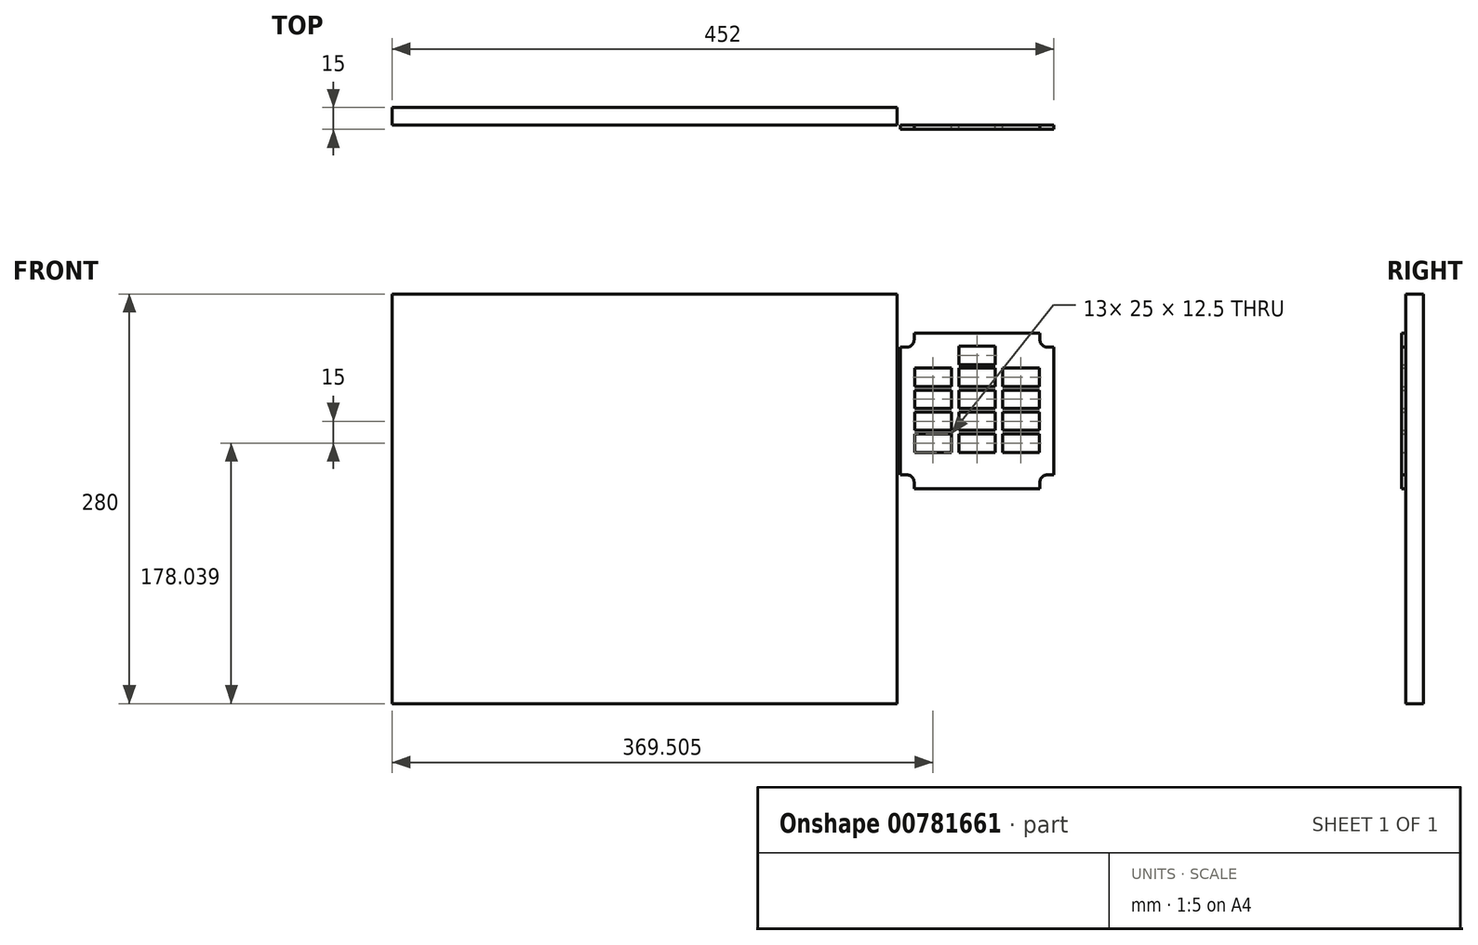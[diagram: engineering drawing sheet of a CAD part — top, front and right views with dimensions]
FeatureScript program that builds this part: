
annotation { "Feature Type Name" : "Feature", "Feature Type Description" : "" }
export const myFeature = defineFeature(function(context is Context, id is Id, definition is map)
    precondition{}
    {
        {
            var Q0;
            Q0=qCreatedBy(makeId("Front.planeOp"),FACE);
            var sketch = newSketch(context, id + "F0", { "sketchPlane" : qUnion([Q0])});
            skLineSegment(sketch, "E0.bottom", {"start": v(172.5, 140) * mm, "end": v(-172.5, 140) * mm});
            skLineSegment(sketch, "E0.top", {"start": v(172.5, -140) * mm, "end": v(-172.5, -140) * mm});
            skLineSegment(sketch, "E0.left", {"start": v(172.5, 140) * mm, "end": v(172.5, -140) * mm});
            skLineSegment(sketch, "E0.right", {"start": v(-172.5, 140) * mm, "end": v(-172.5, -140) * mm});
            skPoint(sketch, "E0.middle", {"position": v(0, 0) * mm});
            skSolve(sketch);
        }
        {
            var Q0;
            Q0=makeQuery(id+"F0.imprint","IMPRINT",FACE,{"disambiguationData":[TD([[makeQuery(id+"F0.imprint","IMPRINT",EDGE,{"derivedFrom":sQuery(id+"F0.wireOp",EDGE,"E0.bottom")}),1.0]])]});
            extrude(context, id + "F1", {"entities" : qUnion([Q0]), "oppositeDirection" : true, "depth" : 12 * mm, "offsetDistance" : 25 * mm});
        }
        {
            var Q0;
            Q0=qCreatedBy(makeId("Front.planeOp"),FACE);
            var sketch = newSketch(context, id + "F2", { "sketchPlane" : qUnion([Q0])});
            skLineSegment(sketch, "E1.bottom", {"start": v(184.03, 113.29) * mm, "end": v(269.98, 113.29) * mm});
            skLineSegment(sketch, "E1.top", {"start": v(184.03, 6.79) * mm, "end": v(269.98, 6.79) * mm});
            skLineSegment(sketch, "E1.left", {"start": v(174.5, 103.76) * mm, "end": v(174.5, 16.31) * mm});
            skLineSegment(sketch, "E1.right", {"start": v(279.5, 103.76) * mm, "end": v(279.5, 16.31) * mm});
            skLineSegment(sketch, "E2.bottom", {"start": v(214.5, 104.29) * mm, "end": v(239.5, 104.29) * mm});
            skLineSegment(sketch, "E2.top", {"start": v(214.5, 91.79) * mm, "end": v(239.5, 91.79) * mm});
            skLineSegment(sketch, "E2.left", {"start": v(214.5, 104.29) * mm, "end": v(214.5, 91.79) * mm});
            skLineSegment(sketch, "E2.right", {"start": v(239.5, 104.29) * mm, "end": v(239.5, 91.79) * mm});
            skLineSegment(sketch, "E3", {"start": v(227, 104.29) * mm, "end": v(227, 102.79) * mm});
            skLineSegment(sketch, "E4.0.1.0", {"start": v(214.5, 89.29) * mm, "end": v(239.5, 89.29) * mm});
            skLineSegment(sketch, "E4.0.1.1", {"start": v(214.5, 89.29) * mm, "end": v(214.5, 76.79) * mm});
            skLineSegment(sketch, "E4.0.1.2", {"start": v(214.5, 76.79) * mm, "end": v(239.5, 76.79) * mm});
            skLineSegment(sketch, "E4.0.1.3", {"start": v(239.5, 89.29) * mm, "end": v(239.5, 76.79) * mm});
            skLineSegment(sketch, "E4.0.2.0", {"start": v(214.5, 74.29) * mm, "end": v(239.5, 74.29) * mm});
            skLineSegment(sketch, "E4.0.2.1", {"start": v(214.5, 74.29) * mm, "end": v(214.5, 61.79) * mm});
            skLineSegment(sketch, "E4.0.2.2", {"start": v(214.5, 61.79) * mm, "end": v(239.5, 61.79) * mm});
            skLineSegment(sketch, "E4.0.2.3", {"start": v(239.5, 74.29) * mm, "end": v(239.5, 61.79) * mm});
            skLineSegment(sketch, "E4.0.3.0", {"start": v(214.5, 59.29) * mm, "end": v(239.5, 59.29) * mm});
            skLineSegment(sketch, "E4.0.3.1", {"start": v(214.5, 59.29) * mm, "end": v(214.5, 46.79) * mm});
            skLineSegment(sketch, "E4.0.3.2", {"start": v(214.5, 46.79) * mm, "end": v(239.5, 46.79) * mm});
            skLineSegment(sketch, "E4.0.3.3", {"start": v(239.5, 59.29) * mm, "end": v(239.5, 46.79) * mm});
            skLineSegment(sketch, "E4.0.4.0", {"start": v(214.5, 44.29) * mm, "end": v(239.5, 44.29) * mm});
            skLineSegment(sketch, "E4.0.4.1", {"start": v(214.5, 44.29) * mm, "end": v(214.5, 31.79) * mm});
            skLineSegment(sketch, "E4.0.4.2", {"start": v(214.5, 31.79) * mm, "end": v(239.5, 31.79) * mm});
            skLineSegment(sketch, "E4.0.4.3", {"start": v(239.5, 44.29) * mm, "end": v(239.5, 31.79) * mm});
            skLineSegment(sketch, "E4.direction1", {"start": v(214.5, 104.29) * mm, "end": v(239.5, 104.29) * mm, "construction": true});
            skLineSegment(sketch, "E4.direction2", {"start": v(214.5, 104.29) * mm, "end": v(214.5, 89.29) * mm, "construction": true});
            skLineSegment(sketch, "E5.1.0.0", {"start": v(244.5, 89.29) * mm, "end": v(244.5, 76.79) * mm});
            skLineSegment(sketch, "E5.1.0.1", {"start": v(244.5, 89.29) * mm, "end": v(269.5, 89.29) * mm});
            skLineSegment(sketch, "E5.1.0.2", {"start": v(244.5, 74.29) * mm, "end": v(269.5, 74.29) * mm});
            skLineSegment(sketch, "E5.1.0.3", {"start": v(244.5, 61.79) * mm, "end": v(269.5, 61.79) * mm});
            skLineSegment(sketch, "E5.1.0.4", {"start": v(244.5, 76.79) * mm, "end": v(269.5, 76.79) * mm});
            skLineSegment(sketch, "E5.1.0.5", {"start": v(244.5, 74.29) * mm, "end": v(244.5, 61.79) * mm});
            skLineSegment(sketch, "E5.1.0.6", {"start": v(269.5, 89.29) * mm, "end": v(269.5, 76.79) * mm});
            skLineSegment(sketch, "E5.1.0.7", {"start": v(269.5, 44.29) * mm, "end": v(269.5, 31.79) * mm});
            skLineSegment(sketch, "E5.1.0.8", {"start": v(244.5, 31.79) * mm, "end": v(269.5, 31.79) * mm});
            skLineSegment(sketch, "E5.1.0.9", {"start": v(244.5, 44.29) * mm, "end": v(244.5, 31.79) * mm});
            skLineSegment(sketch, "E5.1.0.10", {"start": v(244.5, 44.29) * mm, "end": v(269.5, 44.29) * mm});
            skLineSegment(sketch, "E5.1.0.11", {"start": v(269.5, 59.29) * mm, "end": v(269.5, 46.79) * mm});
            skLineSegment(sketch, "E5.1.0.12", {"start": v(244.5, 46.79) * mm, "end": v(269.5, 46.79) * mm});
            skLineSegment(sketch, "E5.1.0.13", {"start": v(244.5, 59.29) * mm, "end": v(244.5, 46.79) * mm});
            skLineSegment(sketch, "E5.1.0.14", {"start": v(244.5, 59.29) * mm, "end": v(269.5, 59.29) * mm});
            skLineSegment(sketch, "E5.1.0.15", {"start": v(269.5, 74.29) * mm, "end": v(269.5, 61.79) * mm});
            skLineSegment(sketch, "E5.direction1", {"start": v(214.5, 31.79) * mm, "end": v(244.5, 31.79) * mm, "construction": true});
            skLineSegment(sketch, "E6.1.0.0", {"start": v(184.5, 74.29) * mm, "end": v(209.5, 74.29) * mm});
            skLineSegment(sketch, "E6.1.0.1", {"start": v(184.5, 61.79) * mm, "end": v(209.5, 61.79) * mm});
            skLineSegment(sketch, "E6.1.0.2", {"start": v(184.5, 89.29) * mm, "end": v(184.5, 76.79) * mm});
            skLineSegment(sketch, "E6.1.0.3", {"start": v(209.5, 44.29) * mm, "end": v(209.5, 31.79) * mm});
            skLineSegment(sketch, "E6.1.0.4", {"start": v(209.5, 89.29) * mm, "end": v(209.5, 76.79) * mm});
            skLineSegment(sketch, "E6.1.0.5", {"start": v(184.5, 89.29) * mm, "end": v(209.5, 89.29) * mm});
            skLineSegment(sketch, "E6.1.0.6", {"start": v(184.5, 31.79) * mm, "end": v(209.5, 31.79) * mm});
            skLineSegment(sketch, "E6.1.0.7", {"start": v(184.5, 44.29) * mm, "end": v(184.5, 31.79) * mm});
            skLineSegment(sketch, "E6.1.0.8", {"start": v(184.5, 74.29) * mm, "end": v(184.5, 61.79) * mm});
            skLineSegment(sketch, "E6.1.0.9", {"start": v(184.5, 76.79) * mm, "end": v(209.5, 76.79) * mm});
            skLineSegment(sketch, "E6.1.0.10", {"start": v(184.5, 44.29) * mm, "end": v(209.5, 44.29) * mm});
            skLineSegment(sketch, "E6.1.0.11", {"start": v(209.5, 59.29) * mm, "end": v(209.5, 46.79) * mm});
            skLineSegment(sketch, "E6.1.0.12", {"start": v(184.5, 46.79) * mm, "end": v(209.5, 46.79) * mm});
            skLineSegment(sketch, "E6.1.0.13", {"start": v(184.5, 59.29) * mm, "end": v(184.5, 46.79) * mm});
            skLineSegment(sketch, "E6.1.0.14", {"start": v(184.5, 59.29) * mm, "end": v(209.5, 59.29) * mm});
            skLineSegment(sketch, "E6.1.0.15", {"start": v(209.5, 74.29) * mm, "end": v(209.5, 61.79) * mm});
            skLineSegment(sketch, "E6.direction1", {"start": v(214.5, 31.79) * mm, "end": v(184.5, 31.79) * mm, "construction": true});
            skLineSegment(sketch, "E7", {"start": v(184.03, 113.29) * mm, "end": v(184.03, 108.53) * mm});
            skLineSegment(sketch, "E8", {"start": v(174.5, 60.04) * mm, "end": v(176.1, 60.04) * mm});
            skArc(sketch, "E9", {"start": v(179.27, 103.76) * mm, "mid": v(182.64, 105.16) * mm, "end": v(184.03, 108.53) * mm});
            skPoint(sketch, "E9.centerSnap0", {"position": v(179.27, 103.76) * mm});
            skPoint(sketch, "E9.centerSnap1", {"position": v(184.03, 108.53) * mm});
            skPoint(sketch, "E10.orphan", {"position": v(174.5, 113.29) * mm});
            skPoint(sketch, "E11.orphan", {"position": v(184.03, 103.76) * mm});
            skLineSegment(sketch, "E12", {"start": v(179.27, 103.76) * mm, "end": v(174.5, 103.76) * mm});
            skArc(sketch, "E13.MirrorCS", {"start": v(274.74, 103.76) * mm, "mid": v(271.37, 105.16) * mm, "end": v(269.98, 108.53) * mm});
            skPoint(sketch, "E14.MirrorP", {"position": v(269.98, 103.76) * mm});
            skPoint(sketch, "E15.MirrorP", {"position": v(269.98, 108.53) * mm});
            skLineSegment(sketch, "E16.MirrorCS", {"start": v(269.98, 113.29) * mm, "end": v(269.98, 108.53) * mm});
            skLineSegment(sketch, "E17.MirrorCS", {"start": v(274.74, 103.76) * mm, "end": v(279.5, 103.76) * mm});
            skPoint(sketch, "E18.MirrorP", {"position": v(274.74, 103.76) * mm});
            skPoint(sketch, "E19.MirrorP", {"position": v(279.5, 113.29) * mm});
            skLineSegment(sketch, "E20.MirrorCS", {"start": v(184.03, 6.79) * mm, "end": v(184.03, 11.55) * mm});
            skLineSegment(sketch, "E21.MirrorCS", {"start": v(179.27, 16.31) * mm, "end": v(174.5, 16.31) * mm});
            skPoint(sketch, "E22.MirrorP", {"position": v(179.27, 16.31) * mm});
            skPoint(sketch, "E23.MirrorP", {"position": v(184.03, 16.31) * mm});
            skPoint(sketch, "E24.MirrorP", {"position": v(184.03, 11.55) * mm});
            skArc(sketch, "E25.MirrorCS", {"start": v(179.27, 16.31) * mm, "mid": v(182.64, 14.92) * mm, "end": v(184.03, 11.55) * mm});
            skPoint(sketch, "E26.MirrorP", {"position": v(174.5, 6.79) * mm});
            skArc(sketch, "E27.MirrorCS", {"start": v(274.74, 16.31) * mm, "mid": v(271.37, 14.92) * mm, "end": v(269.98, 11.55) * mm});
            skPoint(sketch, "E28.MirrorP", {"position": v(269.98, 16.31) * mm});
            skPoint(sketch, "E29.MirrorP", {"position": v(279.5, 6.79) * mm});
            skLineSegment(sketch, "E30.MirrorCS", {"start": v(274.74, 16.31) * mm, "end": v(279.5, 16.31) * mm});
            skPoint(sketch, "E31.MirrorP", {"position": v(274.74, 16.31) * mm});
            skLineSegment(sketch, "E32.MirrorCS", {"start": v(269.98, 6.79) * mm, "end": v(269.98, 11.55) * mm});
            skPoint(sketch, "E33.MirrorP", {"position": v(269.98, 11.55) * mm});
            skSolve(sketch);
        }
        {
            var Q0;
            Q0 = qSketchRegion(id + "F2", true);
            extrude(context, id + "F3", {"entities" : qUnion([Q0]), "depth" : 3 * mm, "offsetDistance" : 25 * mm});
        }
    });
